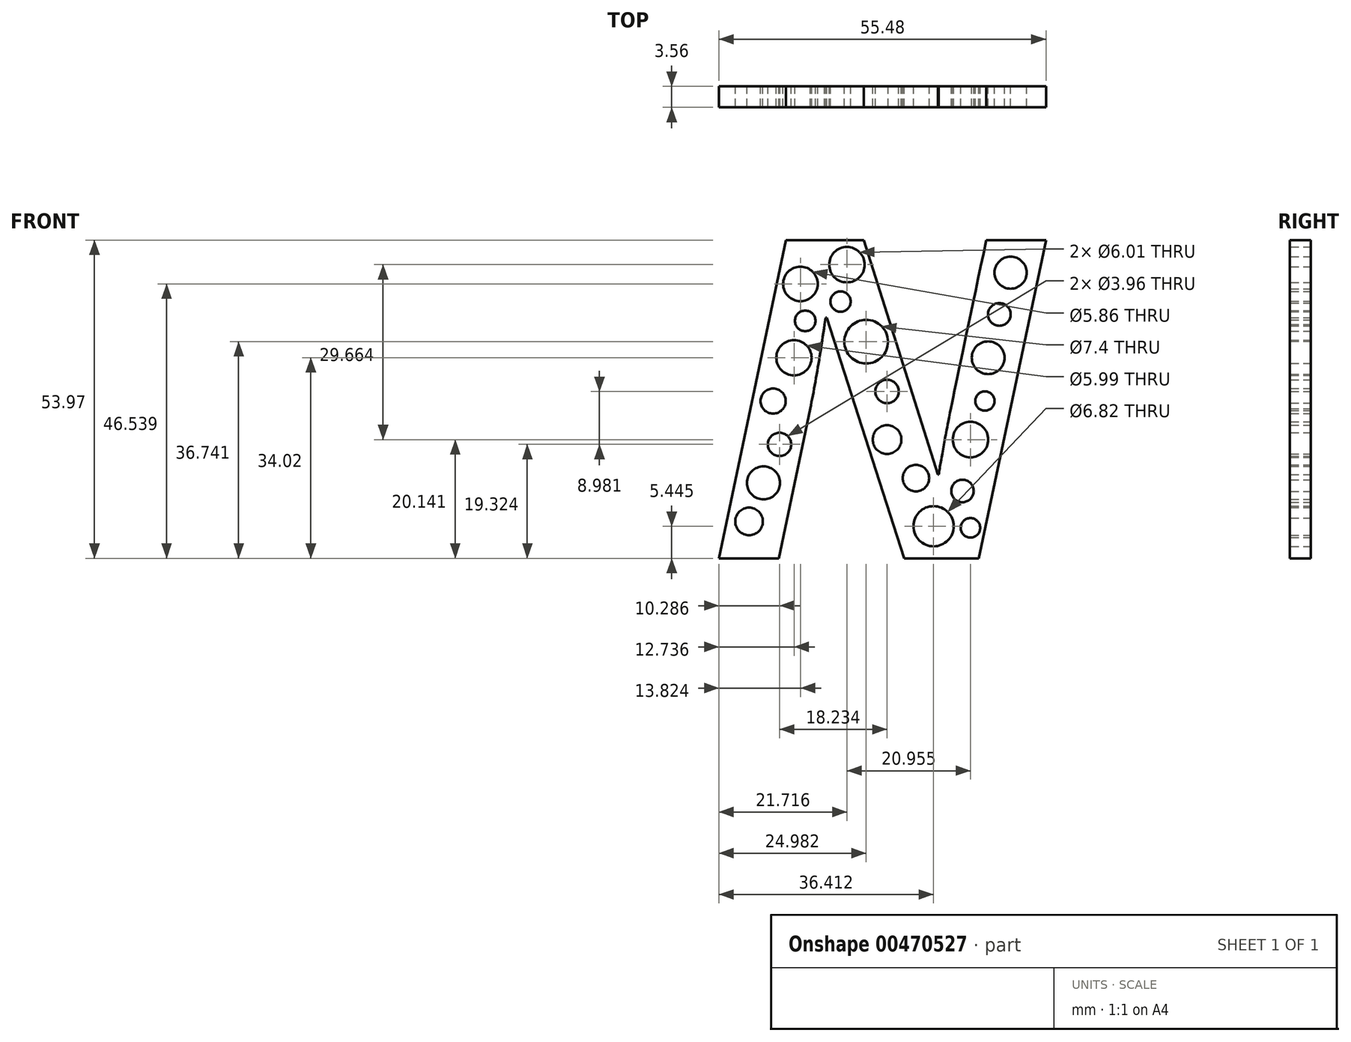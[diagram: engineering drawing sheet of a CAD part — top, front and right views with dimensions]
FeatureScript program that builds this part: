
annotation { "Feature Type Name" : "Feature", "Feature Type Description" : "" }
export const myFeature = defineFeature(function(context is Context, id is Id, definition is map)
    precondition{}
    {
        {
            var Q0;
            Q0=qCreatedBy(makeId("Front.planeOp"),FACE);
            var sketch = newSketch(context, id + "F0", { "sketchPlane" : qUnion([Q0])});
            skText(sketch, "E0", { "text": "N", "fontName": "OpenSans-BoldItalic.ttf"});
            skArc(sketch, "E1", {"start": v(-4.63, 20.41) * mm, "mid": v(-10.75, 29.42) * mm, "end": v(-16.87, 20.41) * mm});
            skArc(sketch, "E2", {"start": v(-7.62, 20.41) * mm, "mid": v(-10.48, 26.62) * mm, "end": v(-13.34, 20.41) * mm});
            const initialGuessF0  = {"E0": [-0.03048, -0.03402, 1, 0, 0.05443]};
            skSetInitialGuess(sketch, initialGuessF0);
            skSolve(sketch);
        }
        {
            var Q0;
            Q0 = qSketchRegion(id + "F0", true);
            extrude(context, id + "F1", {"entities" : qUnion([Q0]), "depth" : 3.56 * mm});
        }
        {
            var Q0;
            Q0=qCreatedBy(makeId("Front.planeOp"),FACE);
            var sketch = newSketch(context, id + "F2", { "sketchPlane" : qUnion([Q0])});
            skCircle(sketch, "E3", {"center": v(-6.8, 15.78) * mm, "radius": 3 * mm});
            skSolve(sketch);
        }
        {
            var Q0;
            Q0 = qSketchRegion(id + "F2", true);
            extrude(context, id + "F3", {"entities" : qUnion([Q0]), "operationType" : NewBodyOperationType.REMOVE, "depth" : 54.86 * mm});
        }
        {
            var Q0;
            Q0=qCreatedBy(makeId("Front.planeOp"),FACE);
            var sketch = newSketch(context, id + "F4", { "sketchPlane" : qUnion([Q0])});
            skCircle(sketch, "E4", {"center": v(20.96, 14.42) * mm, "radius": 2.72 * mm});
            skCircle(sketch, "E5", {"center": v(19.05, 7.35) * mm, "radius": 1.92 * mm});
            skCircle(sketch, "E6", {"center": v(17.14, 0) * mm, "radius": 2.78 * mm});
            skCircle(sketch, "E7", {"center": v(16.6, -7.35) * mm, "radius": 1.63 * mm});
            skCircle(sketch, "E8", {"center": v(14.15, -13.88) * mm, "radius": 3 * mm});
            skCircle(sketch, "E9", {"center": v(12.8, -22.59) * mm, "radius": 1.9 * mm});
            skCircle(sketch, "E10", {"center": v(7.9, -28.58) * mm, "radius": 3.4 * mm});
            skCircle(sketch, "E11", {"center": v(14.15, -28.85) * mm, "radius": 1.66 * mm});
            skCircle(sketch, "E12", {"center": v(4.9, -20.41) * mm, "radius": 2.24 * mm});
            skCircle(sketch, "E13", {"center": v(0, -13.88) * mm, "radius": 2.43 * mm});
            skCircle(sketch, "E14", {"center": v(0, -5.72) * mm, "radius": 1.98 * mm});
            skCircle(sketch, "E15", {"center": v(-3.54, 2.72) * mm, "radius": 3.7 * mm});
            skCircle(sketch, "E16", {"center": v(-23.4, -27.76) * mm, "radius": 2.34 * mm});
            skCircle(sketch, "E17", {"center": v(-20.96, -21.23) * mm, "radius": 2.8 * mm});
            skCircle(sketch, "E18", {"center": v(-18.23, -14.7) * mm, "radius": 1.98 * mm});
            skCircle(sketch, "E19", {"center": v(-19.32, -7.35) * mm, "radius": 2.13 * mm});
            skCircle(sketch, "E20", {"center": v(-15.78, 0) * mm, "radius": 3 * mm});
            skCircle(sketch, "E21", {"center": v(-14.7, 12.52) * mm, "radius": 2.93 * mm});
            skCircle(sketch, "E22", {"center": v(-13.88, 6.26) * mm, "radius": 1.74 * mm});
            skCircle(sketch, "E23", {"center": v(-7.9, 9.53) * mm, "radius": 1.72 * mm});
            skSolve(sketch);
        }
        {
            var Q0;
            Q0 = qSketchRegion(id + "F4", true);
            extrude(context, id + "F5", {"entities" : qUnion([Q0]), "operationType" : NewBodyOperationType.REMOVE, "depth" : 59.44 * mm});
        }
    });
